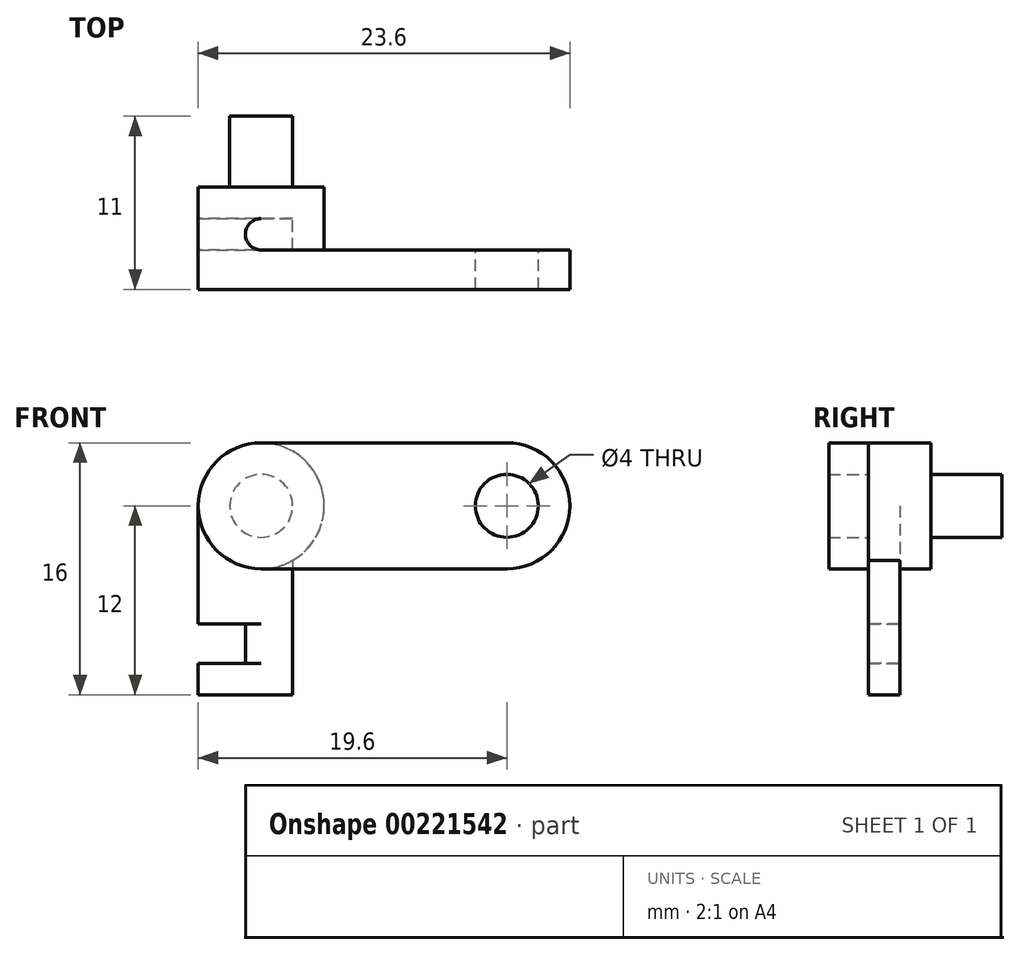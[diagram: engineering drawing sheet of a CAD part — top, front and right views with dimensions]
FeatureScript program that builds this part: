
annotation { "Feature Type Name" : "Feature", "Feature Type Description" : "" }
export const myFeature = defineFeature(function(context is Context, id is Id, definition is map)
    precondition{}
    {
        {
            var Q0;
            Q0=qCreatedBy(makeId("Front.planeOp"),FACE);
            var sketch = newSketch(context, id + "F0", { "sketchPlane" : qUnion([Q0])});
            skCircle(sketch, "E0", {"center": v(0, 0) * mm, "radius": 2 * mm});
            skCircle(sketch, "E1", {"center": v(0, 0) * mm, "radius": 4 * mm});
            skLineSegment(sketch, "E2", {"start": v(0, 4) * mm, "end": v(15.6, 4) * mm});
            skLineSegment(sketch, "E3", {"start": v(0, -4) * mm, "end": v(15.6, -4) * mm});
            skArc(sketch, "E4", {"start": v(15.6, 4) * mm, "mid": v(19.6, 0) * mm, "end": v(15.6, -4) * mm});
            skCircle(sketch, "E5", {"center": v(15.6, 0) * mm, "radius": 2 * mm});
            skLineSegment(sketch, "E6.bottom", {"start": v(2, 0) * mm, "end": v(-4, 0) * mm});
            skLineSegment(sketch, "E6.top", {"start": v(2, -12) * mm, "end": v(-4, -12) * mm});
            skLineSegment(sketch, "E6.left", {"start": v(2, 0) * mm, "end": v(2, -12) * mm});
            skLineSegment(sketch, "E6.right", {"start": v(-4, 0) * mm, "end": v(-4, -12) * mm});
            skLineSegment(sketch, "E7.bottom", {"start": v(-4, -7.5) * mm, "end": v(-1, -7.5) * mm});
            skLineSegment(sketch, "E7.top", {"start": v(-4, -10) * mm, "end": v(-1, -10) * mm});
            skLineSegment(sketch, "E7.left", {"start": v(-4, -7.5) * mm, "end": v(-4, -10) * mm});
            skLineSegment(sketch, "E7.right", {"start": v(-1, -7.5) * mm, "end": v(-1, -10) * mm});
            skSolve(sketch);
        }
        {
            var Q0;
            {var subQ1=sQuery(id+"F0.wireOp",EDGE,"E1");var subQ5=makeQuery(id+"F0.imprint","INTERSECT",VERTEX,{"derivedFrom":[subQ1,sQuery(id+"F0.wireOp",EDGE,"E3")]});Q0=makeQuery(id+"F0.imprint","IMPRINT",FACE,{"disambiguationData":[TD([[makeQuery(id+"F0.imprint","IMPRINT",EDGE,{"disambiguationData":[TD([[subQ5,-1.0]])],"derivedFrom":subQ1}),1.0]])]});}
            var Q1;
            {var subQ0=sQuery(id+"F0.wireOp",EDGE,"E2");var subQ1=sQuery(id+"F0.wireOp",EDGE,"E1");var subQ2=makeQuery(id+"F0.imprint","INTERSECT",VERTEX,{"derivedFrom":[subQ1,subQ0]});Q1=makeQuery(id+"F0.imprint","IMPRINT",FACE,{"disambiguationData":[TD([[makeQuery(id+"F0.imprint","IMPRINT",EDGE,{"disambiguationData":[TD([[subQ2,1.0]])],"derivedFrom":subQ1}),-1.0]])]});}
            var Q2;
            {var subQ1=sQuery(id+"F0.wireOp",EDGE,"E3");Q2=makeQuery(id+"F0.imprint","IMPRINT",FACE,{"disambiguationData":[TD([[makeQuery(id+"F0.imprint","IMPRINT",EDGE,{"derivedFrom":subQ1}),1.0]])]});}
            var Q3;
            {var subQ1=sQuery(id+"F0.wireOp",EDGE,"E1");var subQ5=makeQuery(id+"F0.imprint","INTERSECT",VERTEX,{"derivedFrom":[subQ1,sQuery(id+"F0.wireOp",EDGE,"E2")]});Q3=makeQuery(id+"F0.imprint","IMPRINT",FACE,{"disambiguationData":[TD([[makeQuery(id+"F0.imprint","IMPRINT",EDGE,{"disambiguationData":[TD([[subQ5,1.0]])],"derivedFrom":subQ1}),1.0]])]});}
            var Q4;
            {var subQ0=sQuery(id+"F0.wireOp",EDGE,"SoTTxwFc-vS4E-siD4-y6u4-lvNVkrnug5Sc.bottom");var subQ1=sQuery(id+"F0.wireOp",EDGE,"E0");var subQ3=makeQuery(id+"F0.imprint","INTERSECT",VERTEX,{"derivedFrom":[subQ1,subQ0]});Q4=makeQuery(id+"F0.imprint","IMPRINT",FACE,{"disambiguationData":[TD([[makeQuery(id+"F0.imprint","IMPRINT",EDGE,{"disambiguationData":[TD([[subQ3,1.0]])],"derivedFrom":subQ1}),1.0]])]});}
            var Q5;
            {var subQ0=sQuery(id+"F0.wireOp",EDGE,"SoTTxwFc-vS4E-siD4-y6u4-lvNVkrnug5Sc.bottom");var subQ1=sQuery(id+"F0.wireOp",EDGE,"E0");var subQ3=makeQuery(id+"F0.imprint","INTERSECT",VERTEX,{"derivedFrom":[subQ1,subQ0]});Q5=makeQuery(id+"F0.imprint","IMPRINT",FACE,{"disambiguationData":[TD([[makeQuery(id+"F0.imprint","IMPRINT",EDGE,{"disambiguationData":[TD([[subQ3,-1.0]])],"derivedFrom":subQ1}),1.0]])]});}
            extrude(context, id + "F1", {"entities" : qUnion([Q0, Q1, Q2, Q3, Q4, Q5]), "depth" : 2.5 * mm});
        }
        {
            var Q0;
            {var subQ1=sQuery(id+"F0.wireOp",EDGE,"E1");var subQ5=makeQuery(id+"F0.imprint","INTERSECT",VERTEX,{"derivedFrom":[subQ1,sQuery(id+"F0.wireOp",EDGE,"E2")]});Q0=makeQuery(id+"F0.imprint","IMPRINT",FACE,{"disambiguationData":[TD([[makeQuery(id+"F0.imprint","IMPRINT",EDGE,{"disambiguationData":[TD([[subQ5,1.0]])],"derivedFrom":subQ1}),1.0]])]});}
            var Q1;
            {var subQ1=sQuery(id+"F0.wireOp",EDGE,"E1");var subQ5=makeQuery(id+"F0.imprint","INTERSECT",VERTEX,{"derivedFrom":[subQ1,sQuery(id+"F0.wireOp",EDGE,"E3")]});Q1=makeQuery(id+"F0.imprint","IMPRINT",FACE,{"disambiguationData":[TD([[makeQuery(id+"F0.imprint","IMPRINT",EDGE,{"disambiguationData":[TD([[subQ5,-1.0]])],"derivedFrom":subQ1}),1.0]])]});}
            extrude(context, id + "F2", {"entities" : qUnion([Q0, Q1]), "operationType" : NewBodyOperationType.ADD, "oppositeDirection" : true, "depth" : 4 * mm});
        }
        {
            var Q0;
            {var subQ0=sQuery(id+"F0.wireOp",EDGE,"SoTTxwFc-vS4E-siD4-y6u4-lvNVkrnug5Sc.bottom");var subQ1=sQuery(id+"F0.wireOp",EDGE,"E0");var subQ3=makeQuery(id+"F0.imprint","INTERSECT",VERTEX,{"derivedFrom":[subQ1,subQ0]});Q0=makeQuery(id+"F0.imprint","IMPRINT",FACE,{"disambiguationData":[TD([[makeQuery(id+"F0.imprint","IMPRINT",EDGE,{"disambiguationData":[TD([[subQ3,1.0]])],"derivedFrom":subQ1}),1.0]])]});}
            var Q1;
            {var subQ0=sQuery(id+"F0.wireOp",EDGE,"SoTTxwFc-vS4E-siD4-y6u4-lvNVkrnug5Sc.bottom");var subQ1=sQuery(id+"F0.wireOp",EDGE,"E0");var subQ3=makeQuery(id+"F0.imprint","INTERSECT",VERTEX,{"derivedFrom":[subQ1,subQ0]});Q1=makeQuery(id+"F0.imprint","IMPRINT",FACE,{"disambiguationData":[TD([[makeQuery(id+"F0.imprint","IMPRINT",EDGE,{"disambiguationData":[TD([[subQ3,-1.0]])],"derivedFrom":subQ1}),1.0]])]});}
            extrude(context, id + "F3", {"entities" : qUnion([Q0, Q1]), "operationType" : NewBodyOperationType.ADD, "oppositeDirection" : true, "depth" : 8.5 * mm});
        }
        {
            var Q0;
            {var subQ0=sQuery(id+"F0.wireOp",EDGE,"E6.bottom");var subQ1=sQuery(id+"F0.wireOp",EDGE,"E0");var subQ3=makeQuery(id+"F0.imprint","INTERSECT",VERTEX,{"derivedFrom":[subQ1,subQ0]});Q0=makeQuery(id+"F0.imprint","IMPRINT",FACE,{"disambiguationData":[TD([[makeQuery(id+"F0.imprint","IMPRINT",EDGE,{"disambiguationData":[TD([[subQ3,1.0]])],"derivedFrom":subQ1}),1.0]])]});}
            var Q1;
            {var subQ0=sQuery(id+"F0.wireOp",EDGE,"E6.bottom");var subQ1=sQuery(id+"F0.wireOp",EDGE,"E0");var subQ3=makeQuery(id+"F0.imprint","INTERSECT",VERTEX,{"derivedFrom":[subQ1,subQ0]});Q1=makeQuery(id+"F0.imprint","IMPRINT",FACE,{"disambiguationData":[TD([[makeQuery(id+"F0.imprint","IMPRINT",EDGE,{"disambiguationData":[TD([[subQ3,-1.0]])],"derivedFrom":subQ1}),1.0]])]});}
            var Q2;
            {var subQ1=sQuery(id+"F0.wireOp",EDGE,"E1");var subQ5=makeQuery(id+"F0.imprint","INTERSECT",VERTEX,{"derivedFrom":[subQ1,sQuery(id+"F0.wireOp",EDGE,"E3")]});Q2=makeQuery(id+"F0.imprint","IMPRINT",FACE,{"disambiguationData":[TD([[makeQuery(id+"F0.imprint","IMPRINT",EDGE,{"disambiguationData":[TD([[subQ5,-1.0]])],"derivedFrom":subQ1}),1.0]])]});}
            var Q3;
            {var subQ0=sQuery(id+"F0.wireOp",EDGE,"E3");var subQ1=sQuery(id+"F0.wireOp",EDGE,"E1");var subQ2=makeQuery(id+"F0.imprint","INTERSECT",VERTEX,{"derivedFrom":[subQ1,subQ0]});Q3=makeQuery(id+"F0.imprint","IMPRINT",FACE,{"disambiguationData":[TD([[makeQuery(id+"F0.imprint","IMPRINT",EDGE,{"disambiguationData":[TD([[subQ2,-1.0]])],"derivedFrom":subQ1}),-1.0]])]});}
            var Q4;
            {var subQ0=sQuery(id+"F0.wireOp",EDGE,"E6.top");Q4=makeQuery(id+"F0.imprint","IMPRINT",FACE,{"disambiguationData":[TD([[makeQuery(id+"F0.imprint","IMPRINT",EDGE,{"derivedFrom":subQ0}),-1.0]])]});}
            extrude(context, id + "F4", {"entities" : qUnion([Q0, Q1, Q2, Q3, Q4]), "operationType" : NewBodyOperationType.ADD, "oppositeDirection" : true, "depth" : 2 * mm});
        }
        {
            var Q0;
            Q0=makeQuery(id+"F4.opExtrude","CAP_EDGE",EDGE,{"disambiguationData":[OSD([sQuery(id+"F0.wireOp",EDGE,"E7.right")])],"isStart":false});
            var Q1;
            Q1=makeQuery(id+"F4.opExtrude","CAP_EDGE",EDGE,{"disambiguationData":[OSD([sQuery(id+"F0.wireOp",EDGE,"E7.right")])],"isStart":true});
            fillet(context, id + "F5", {"entities" : qUnion([Q0, Q1]), "radius" : 1 * mm, "tangentPropagation" : true, "allowEdgeOverflow" : false});
        }
    });
